# Revit family: ShowerMixer-(Built-in-Exposedpart)-WithHandshower-Vitra-İstanbulSeries-A41802-1
name_source: partatom
category: Plumbing Fixtures
revit_build: Autodesk Revit 2017 (Build: 20160225_1515(x64)
units: mm (PartAtom-declared; Revit-internal decimal feet)

## family parameters
Cut with Voids When Loaded = No
Host = Face
OmniClass Number = 23.45.00.00
OmniClass Title = Sanitary, Laundry, and Cleaning Equipment
Part Type = Normal
Room Calculation Point = No
Round Connector Dimension = Use Diameter
Shared = Yes

## types (12) — shared parameters
BIMobject category = Bath/Shower Mixer
Brand = VitrA
CW Connection = Yes
Default Elevation = 850 mm  [stored 2.78871 ft]
Description = İstanbul  Built-in Shower Mixer (Exposed Part)
Design country = Turkey
HW Connection = Yes
Hot Water Supply (max.) = 80 °C
Hot Water temperature, factory set to = 38 °C
IFC Classification = Sanitary Terminal
Main Material = Brass
Manufacturer = Vitra
Manufacturer name = Vitra
Masterformat 2014 Code = 22 40 00
Masterformat 2014 Description = Plumbing Fixtures
Min. flow pressure of = 0.5 bar
NBS Referans Code = 45-35-70/315
NBS Referans Description = Water supply fittings for baths
Nominal Depth (mm) = 245 mm  [stored 0.803806 ft]
Nominal Height (mm) = 600 mm
Nominal Width (mm) = 250 mm
Number Of Connections = 2
OmniClass Code = 23.45.55.17
OmniClass Description = Mixing Faucets
Primary Material = <By Category>
Product Type = Built-in Shower mixer (exposed part)
Product certification = https://www.vitraglobal.com
Product family = İstanbul
Product group = Shower Mixer (exposed part)
Range of Hot Water Supply = 5 - 65 °C
Range of flow pressure = 1 - 5 bar
Technical description = https://www.vitraglobal.com
Test Pressure = 16 bar
URL = https://vitraglobal.com
Uniclass 1.4 Code = L725111
Uniclass 1.4 Description = Mixer taps
Uniclass 2.0 Code = Pr_40_20_87_09
Uniclass 2.0 Description = Bath taps
Uniclass 2015 Code = Pr_40_20_87_09
Uniclass 2015 Name = Bath taps
Uniformat II Code = 22 40 00
Uniformat II Description = Plumbing Fixture
Vent Connection = No
Waste Connection = Yes
Weight Net (kg) = 6.5
Youtube = https://www.youtube.com
zero-valued in all types: Connection Diameter (mm)

## per-type parameters (varying)
| type | Article No. (default) | Coating Material | Color | Model | Product SKU | Product data url | Product url | Warranty Period (Year) |
| ShowerMixer(Built-in)-Vitra-İstanbulSeries-A41802VUK | A41802VUK | Chrome | Chrome | A41802VUK | A41802VUK | https://www.vitraglobal.com |  | 7 Years |
| ShowerMixer(Built-in)-Vitra-İstanbulSeries-A41802EXP | A41802EXP | Chrome | Chrome | A41802EXP | A41802EXP | https://www.vitraglobal.com |  | 7 Years |
| ShowerMixer(Built-in)-Vitra-İstanbulSeries-A41802EKM | A41802EKM | Chrome | Chrome | A41802EKM | A41802EKM | https://www.vitraglobal.com |  | 7 Years |
| ShowerMixer(Built-in)-Vitra-İstanbulSeries-A4180299EXP | A4180299EXP | White | White | A4180299EXP | A4180299EXP | https://www.vitraglobal.com |  | 7 Years |
| ShowerMixer(Built-in)-Vitra-İstanbulSeries-A4180299 | A4180299 | White | White | A4180299 | A4180299 | https://www.vitraglobal.com |  | 10 Years |
| ShowerMixer(Built-in)-Vitra-İstanbulSeries-A4180292EXP | A4180292EXP | Black | Black | A4180292EXP | A4180292EXP | https://www.vitraglobal.com |  | 7 Years |
| ShowerMixer(Built-in)-Vitra-İstanbulSeries-A4180292 | A4180292 | Black | Black | A4180292 | A4180292 | https://www.vitraglobal.com |  | 10 Years |
| ShowerMixer(Built-in)-Vitra-İstanbulSeries-A4180223VUK | A4180223VUK | Gold | Gold | A4180223VUK | A4180223VUK | https://www.vitraglobal.com |  | 7 Years |
| ShowerMixer(Built-in)-Vitra-İstanbulSeries-A4180223EXP | A4180223EXP | Gold | Gold | A4180223EXP | A4180223EXP | https://www.vitraglobal.com |  | 7 Years |
| ShowerMixer(Built-in)-Vitra-İstanbulSeries-A4180223EKM | A4180223EKM | Gold | Gold | A4180223EKM | A4180223EKM | https://www.vitraglobal.com |  | 7 Years |
| ShowerMixer(Built-in)-Vitra-İstanbulSeries-A4180223 | A41802 | Gold | Gold | A41802 | A41802 | https://www.vitraglobal.com |  | 10 Years |
| ShowerMixer(Built-in)-Vitra-İstanbulSeries-A41802 | A41802 | Chrome | Chrome | A41802 | A41802 | https://www.bimobject.com | https://www.vitraglobal.com | 10 Years |

note: [stored X ft] marks values corroborated as IEEE doubles in the binary element streams (Revit-internal decimal feet)

## geometry (parser evidence)
native form markers: Sweep x2
no freeform markers — native parametric forms only
